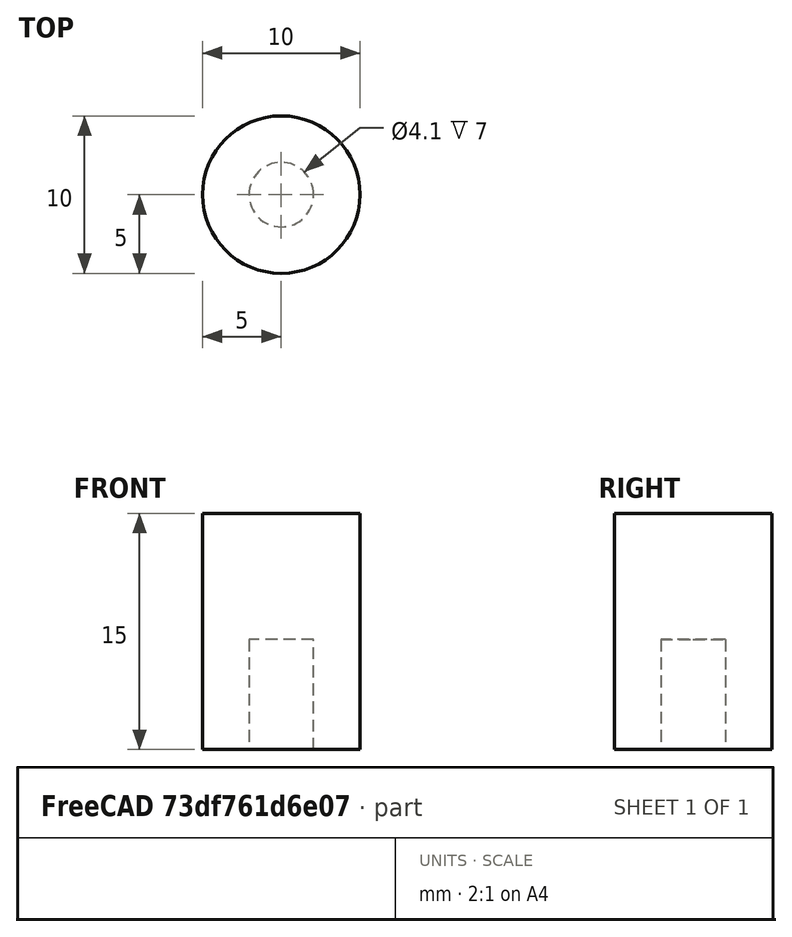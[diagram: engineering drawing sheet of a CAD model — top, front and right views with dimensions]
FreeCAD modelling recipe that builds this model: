
FCSTD DOCUMENT  (FreeCAD 1.0R39319 (Git))
Label: 03_frame_sleeve
License: All rights reserved
LicenseURL: http://en.wikipedia.org/wiki/All_rights_reserved
objects: TechDraw::DrawViewDimension×5, TechDraw::DrawProjGroupItem×4, Sketcher::SketchObject×2, TechDraw::DrawViewAnnotation×2, PartDesign::Pad×1, PartDesign::Pocket×1, PartDesign::Body×1, TechDraw::DrawSVGTemplate×1, TechDraw::DrawProjGroup×1, TechDraw::DrawViewBalloon×1, TechDraw::DrawPage×1
note: 17 computed .brp shape members not serialized (recipe doc carries the construction recipe); baked Part::Feature solids carry a one-line shape summary decoded from their .brp

FEATURE [Sketcher::SketchObject] Sketch
  ArcFitTolerance = 1e-06
  AttachmentSupport = -> [XY_Plane]
  FullyConstrained = true
  MakeInternals = false
  MapMode = 5
  sketch-geometry (1):
    g0: Circle CenterX=0 CenterY=0 CenterZ=0 NormalX=0 NormalY=0 NormalZ=1 AngleXU=0 Radius=5
  constraints (2):
    c: Coincident(g0,g-1)
    c: Diameter(g0) = 10
FEATURE [PartDesign::Pad] Pad
  Direction = (0,0,1)
  Length = 15
  Length2 = 10
  Profile = -> Sketch
  ReferenceAxis = -> Sketch [N_Axis]
  Suppressed = false
  Type = 0
FEATURE [Sketcher::SketchObject] Sketch001
  ArcFitTolerance = 1e-06
  AttachmentSupport = -> [XY_Plane]
  FullyConstrained = true
  MakeInternals = false
  MapMode = 5
  sketch-geometry (1):
    g0: Circle CenterX=0 CenterY=0 CenterZ=0 NormalX=0 NormalY=0 NormalZ=1 AngleXU=0 Radius=2.05
  constraints (2):
    c: Coincident(g0,g-1)
    c: Diameter(g0) = 4.1
FEATURE [PartDesign::Pocket] Pocket
  BaseFeature = -> Pad
  Direction = (0,0,-1)
  Length = 7
  Length2 = 5
  Profile = -> Sketch001
  ReferenceAxis = -> Sketch001 [N_Axis]
  Reversed = true
  Suppressed = false
  Type = 0
FEATURE [PartDesign::Body] Body
  AllowCompound = false
  Group = -> [Sketch,Pad,Sketch001,Pocket]
  Origin = -> Origin
  Tip = -> Pocket
FEATURE [TechDraw::DrawSVGTemplate] Template
  EditableTexts = AuthorName=Matthias Mosimann; CheckDate=N/A; CreationDate=15/04/2026; DrawingNumber=1.0; FC-Title=Hülse für Rahmen; SheetNumber=1 / 1; SupervisorName=N/A; Weight=N/A; scale=2 : 1
  Height = 297
  Orientation = 1
  Template = C:/Program Files/FreeCAD 1.0/data/Mod/TechDraw/Templates/A3_Landscape_TD.svg
  Width = 420
FEATURE [TechDraw::DrawProjGroupItem] View  label="Front"
  CoarseView = false
  Direction = (0,-1,0)
  Focus = 100
  HardHidden = false
  IsoCount = 0
  IsoHidden = false
  IsoVisible = false
  LockPosition = true
  Perspective = false
  Rotation = 0
  RotationVector = (1,0,0)
  Scale = 2
  ScaleType = 2
  ScrubCount = 1
  SeamHidden = false
  SeamVisible = true
  SmoothHidden = false
  SmoothVisible = true
  Source = -> [Body]
  Type = 0
  X = 0
  XDirection = (1,0,0)
  Y = 0
FEATURE [TechDraw::DrawProjGroupItem] ProjItem  label="Left"
  CoarseView = false
  Direction = (-1,-1e-16,0)
  Focus = 100
  HardHidden = true
  IsoCount = 0
  IsoHidden = false
  IsoVisible = false
  LockPosition = true
  Perspective = false
  Rotation = 0
  RotationVector = (1,0,0)
  Scale = 2
  ScaleType = 0
  ScrubCount = 1
  SeamHidden = false
  SeamVisible = true
  SmoothHidden = false
  SmoothVisible = true
  Source = -> [Body]
  Type = 1
  X = 50
  XDirection = (1e-16,-1,0)
  Y = 0
FEATURE [TechDraw::DrawProjGroupItem] ProjItem001  label="Bottom"
  CoarseView = false
  Direction = (0,0,-1)
  Focus = 100
  HardHidden = false
  IsoCount = 0
  IsoHidden = false
  IsoVisible = false
  LockPosition = true
  Perspective = false
  Rotation = 0
  RotationVector = (1,0,0)
  Scale = 2
  ScaleType = 0
  ScrubCount = 1
  SeamHidden = false
  SeamVisible = true
  SmoothHidden = false
  SmoothVisible = true
  Source = -> [Body]
  Type = 5
  X = 0
  XDirection = (1,0,0)
  Y = 55
FEATURE [TechDraw::DrawProjGroupItem] ProjItem002  label="Top"
  CoarseView = false
  Direction = (0,0,1)
  Focus = 100
  HardHidden = false
  IsoCount = 0
  IsoHidden = false
  IsoVisible = false
  LockPosition = true
  Perspective = false
  Rotation = 0
  RotationVector = (1,0,0)
  Scale = 2
  ScaleType = 0
  ScrubCount = 1
  SeamHidden = false
  SeamVisible = true
  SmoothHidden = false
  SmoothVisible = true
  Source = -> [Body]
  Type = 4
  X = 0
  XDirection = (1,0,0)
  Y = -55
FEATURE [TechDraw::DrawProjGroup] ProjGroup
  Anchor = -> View
  AutoDistribute = true
  LockPosition = false
  ProjectionType = 0
  Rotation = 0
  Scale = 2
  ScaleType = 2
  Source = -> [Body]
  Views = -> [View,ProjItem,ProjItem001,ProjItem002]
  X = 150.687
  Y = 158.223
  spacingX = 30
  spacingY = 30
FEATURE [TechDraw::DrawViewDimension] Dimension
  AngleOverride = false
  Arbitrary = false
  ArbitraryTolerances = false
  BoxCorners = (2) [(-10,-10,0),(10,10,0)]
  EqualTolerance = true
  ExtensionAngle = 0
  FormatSpec = ⌀%.2w
  FormatSpecOverTolerance = %+.2w
  FormatSpecUnderTolerance = %+.2w
  Inverted = false
  LineAngle = 0
  LockPosition = false
  MeasureType = 1
  OverTolerance = 0
  References2D = -> [ProjItem001]
  Rotation = 0
  ScaleType = 0
  TheoreticalExact = false
  Type = 5
  UnderTolerance = 0
  X = -46.139
  Y = 8.07909
FEATURE [TechDraw::DrawViewDimension] Dimension001
  AngleOverride = false
  Arbitrary = false
  ArbitraryTolerances = false
  BoxCorners = (2) [(-10,-10,0),(10,10,0)]
  EqualTolerance = true
  ExtensionAngle = 0
  FormatSpec = ⌀%.2w
  FormatSpecOverTolerance = %+.2w
  FormatSpecUnderTolerance = %+.2w
  Inverted = false
  LineAngle = 0
  LockPosition = false
  MeasureType = 1
  OverTolerance = 0
  References2D = -> [ProjItem001]
  Rotation = 0
  ScaleType = 0
  TheoreticalExact = false
  Type = 5
  UnderTolerance = 0
  X = -40.3274
  Y = 19.1595
FEATURE [TechDraw::DrawViewDimension] Dimension002
  AngleOverride = false
  Arbitrary = false
  ArbitraryTolerances = false
  BoxCorners = (2) [(-10,-15,-1e-07),(10,15,1e-07)]
  EqualTolerance = true
  ExtensionAngle = 0
  FormatSpec = %.2w
  FormatSpecOverTolerance = %+.2w
  FormatSpecUnderTolerance = %+.2w
  Inverted = false
  LineAngle = 0
  LockPosition = false
  MeasureType = 1
  OverTolerance = 0
  References2D = -> [ProjItem]
  Rotation = 0
  ScaleType = 0
  TheoreticalExact = false
  Type = 2
  UnderTolerance = 0
  X = 34.4112
  Y = -8
FEATURE [TechDraw::DrawViewDimension] Dimension003
  AngleOverride = false
  Arbitrary = false
  ArbitraryTolerances = false
  BoxCorners = (2) [(-10,-15,-1e-07),(10,15,1e-07)]
  EqualTolerance = true
  ExtensionAngle = 0
  FormatSpec = %.2w
  FormatSpecOverTolerance = %+.2w
  FormatSpecUnderTolerance = %+.2w
  Inverted = false
  LineAngle = 0
  LockPosition = false
  MeasureType = 1
  OverTolerance = 0
  References2D = -> [ProjItem]
  Rotation = 0
  ScaleType = 0
  TheoreticalExact = false
  Type = 2
  UnderTolerance = 0
  X = -27.1693
  Y = 0
FEATURE [TechDraw::DrawViewDimension] Dimension004
  AngleOverride = false
  Arbitrary = false
  ArbitraryTolerances = false
  BoxCorners = (2) [(-10,-15,-1e-07),(10,15,1e-07)]
  EqualTolerance = true
  ExtensionAngle = 0
  FormatSpec = %.2w
  FormatSpecOverTolerance = %+.2w
  FormatSpecUnderTolerance = %+.2w
  Inverted = false
  LineAngle = 0
  LockPosition = false
  MeasureType = 1
  OverTolerance = 0
  References2D = -> [ProjItem]
  Rotation = 0
  ScaleType = 0
  TheoreticalExact = false
  Type = 0
  UnderTolerance = 0
  X = 22.1267
  Y = -26.0991
FEATURE [TechDraw::DrawViewAnnotation] Annotation
  Font = osifont
  LineSpace = 80
  LockPosition = false
  MaxWidth = 120
  Rotation = 0
  Scale = 0.5
  ScaleType = 1
  Text = (1) Hülse hat 7mm Sackloch. damit 9mm Stift aufsteht. Ausserdem hat die Sacklochbohrung 4.1mm Durchmesser, damit die Lamelle frei beweglich ist.
  TextSize = 3
  TextStyle = 0
  X = 330.887
  Y = 151.302
FEATURE [TechDraw::DrawViewBalloon] Balloon
  BubbleShape = 0
  EndType = 0
  EndTypeScale = 1
  KinkLength = 5
  LockPosition = false
  OriginX = 2.05
  OriginY = -4
  Rotation = 0
  ScaleType = 0
  ShapeScale = 1
  SourceView = -> ProjItem
  Text = 1
  TextWrapLen = -1
  X = 12.05
  Y = 6
FEATURE [TechDraw::DrawViewAnnotation] Annotation005
  Font = osifont
  LineSpace = 80
  LockPosition = false
  MaxWidth = 120
  Rotation = 0
  Scale = 0.5
  ScaleType = 1
  Text = Hülse ist aus Edelstahl. | 3D Ansichten können von der angegebenen Skalierungsgrösse abweichen. | Alle Angaben in mm.
  TextSize = 3
  TextStyle = 1
  X = 330.887
  Y = 189.946
FEATURE [TechDraw::DrawPage] Page
  KeepUpdated = true
  NextBalloonIndex = 2
  ProjectionType = 0
  Template = -> Template
  Views = -> [ProjGroup,Dimension,Dimension001,Dimension002,Dimension003,Dimension004,Annotation,Balloon,Annotation005]
